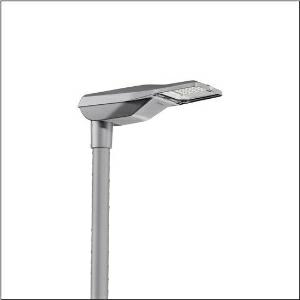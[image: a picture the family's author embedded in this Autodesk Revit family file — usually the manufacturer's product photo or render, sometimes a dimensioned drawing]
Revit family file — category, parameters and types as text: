
# Revit family: streetlight_sl_21_iq_micro___st0_8a_5xe1c31g08db_5951
name_source: partatom
category: Lighting Fixtures
units: mm (PartAtom-declared; Revit-internal decimal feet)

## family parameters
Cut with Voids When Loaded = No
Host = Face
Light Source = No
Part Type = Normal
Room Calculation Point = No
Round Connector Dimension = Use Diameter
Shared = No

## types (1)
- --- (1 x LED, 4810 lm, 36.4 W, 3000K)
    Apparent Load = 36 VA
    CIE Flux Codes = 38 75 97 100 100
    Color Rendering = 70
    Color Temperature = 3000K
    Default Elevation = 1800 mm
    Description = Streetlight SL 21 iQ micro, mast luminaire, primary light control with lens, of PMMA, primary optical cover: cover, of toughened safety glass, transparent, light distribution: ST0.8a, light emission: direct distribution, primary light characteristic: asymmetric, installation type: post-top, side-entry, LED, High Power LED, rated luminous flux: 4.810lm, luminous efficacy: 132lm/W, light colour: 730, colour temperature: 3000K, control gear: iQ Street-Remote, control: Street-Remote, Auto-Match, Temp-Guard, Lumen-Switch, Night-Set, Smart-Wire, Light-Fading, Desk-Remote (wireless, voltage-free reading and setting of iQ features in the workshop via application-optimized NFC function/RFID function), optimised constant luminous flux control (CLO 2.0), pre-setting: linear dimming characteristic, mains connection: 220..240V, AC, 50/60Hz, start of lifetime: 36W, end of service life: 38W, reduction: 16W, luminaire housing, of diecast aluminium, powder-coated, SITECO metallic grey (DB 702S), corrosivity category C5 high according to DIN EN ISO 12944, please order mast flange separately, inclination adjustable: 0°, 5°, 10°, 15°, sealing non-destructively replaceable, multi-level sealing system, length: 528mm, width: 235mm, height: 110mm, mast flange for spigot size: 42mm (side-entry): 5XC10008XM4, 60/48mm (side-entry/post-top): 5XC10108XM2, 76/60mm (side-entry/post-top): 5XC10108XM1, protection rating (complete): IP66, insulation class (complete): insulation class II (safety insulation), certification: CE, ENEC, ENEC+, VDE, impact resistance: IK10, permissible operating ambient temperature for outdoor applications: -40..+50°C, standard-compliant lighting for roads and squares, packaging unit: 1 piece

Light Distribution: ST0.8a
    Height = 110 mm
    Lamp = 1 x LED
    Lamp Light Flux = 4810 lm
    Lamp Power = 36.4 W
    Lamp count = 1
    Length = 528 mm
    Luminous efficacy = 132 lm/W
    Manufacturer = Siteco
    ModVariant = No
    Model = 5XE1C31G08DB
    Number of Poles = 1
    OnlyDefault = Yes
    Power Factor = 1
    Product Name = Streetlight SL 21 iQ micro | ST0.8a
    Product group = mast luminaire | pylon top
    ProductGroupID = 6100
    Protection Class = Protection class II
    Protection Degree = IP 66
    RLX_Detail_Level = 1
    RLX_Emergency_Light_Flux = 0 lm
    RLX_Emergency_Type = 0
    RLX_Emergency_Type_DB = No
    RlxData = <blob elided: 99229 chars, md5=422a914b>
    Socket = socket
    Standby Power = 0 W
    System Light Flux = 4810 lm
    System Power = 36 W
    Type Comments = factory setting: luminous flux: 100 % | dim-lin: 254 | 715 mA
    Type Image = l_1006881.jpg
    URL = http://relux.com
    VarID = @adj_154033
    Voltage = 0 V
    Weight = 0.00 kg
    Width = 235 mm

## geometry (parser evidence)
native form markers: Blend x4, Sweep x9
no freeform markers — native parametric forms only
